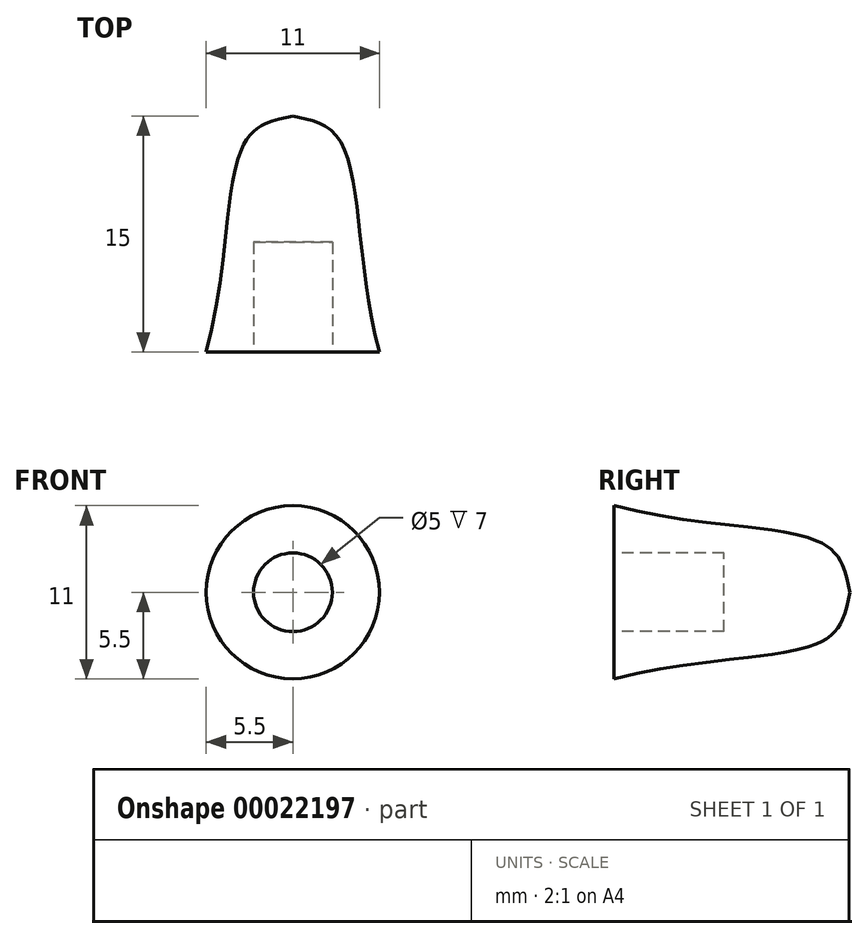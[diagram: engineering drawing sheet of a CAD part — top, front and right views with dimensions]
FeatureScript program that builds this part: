
annotation { "Feature Type Name" : "Feature", "Feature Type Description" : "" }
export const myFeature = defineFeature(function(context is Context, id is Id, definition is map)
    precondition{}
    {
        {
            var Q0;
            Q0=qCreatedBy(makeId("Top.planeOp"),FACE);
            var sketch = newSketch(context, id + "F0", { "sketchPlane" : qUnion([Q0])});
            skLineSegment(sketch, "E0.bottom", {"start": v(2.5, 0) * mm, "end": v(5.5, 0) * mm});
            skLineSegment(sketch, "E0.left", {"start": v(0, 7) * mm, "end": v(0, 15) * mm});
            skFitSpline(sketch, "E1", {"points": [v(0, 15) * mm, v(2.9, 13.57) * mm, v(5.5, 0) * mm], "startDerivative": vector(9.3, -1.95) * mm, "endDerivative": vector(6.75, -25.27) * mm});
            skLineSegment(sketch, "E2.top", {"start": v(0, 7) * mm, "end": v(2.5, 7) * mm});
            skLineSegment(sketch, "E2.right", {"start": v(2.5, 0) * mm, "end": v(2.5, 7) * mm});
            skPoint(sketch, "E0.right.end.orphan", {"position": v(5.5, 15) * mm});
            skPoint(sketch, "E2.left.start.orphan", {"position": v(0, 0) * mm});
            skSolve(sketch);
        }
        {
            var Q0;
            Q0=qSketchRegion(id+"F0",true);
            var Q1;
            Q1=sQuery(id+"F0.wireOp",EDGE,"E0.left");
            revolve(context, id + "F1", {"entities" : qUnion([Q0]), "axis" : qUnion([Q1]), "revolveType" : RevolveType.FULL});
        }
    });
